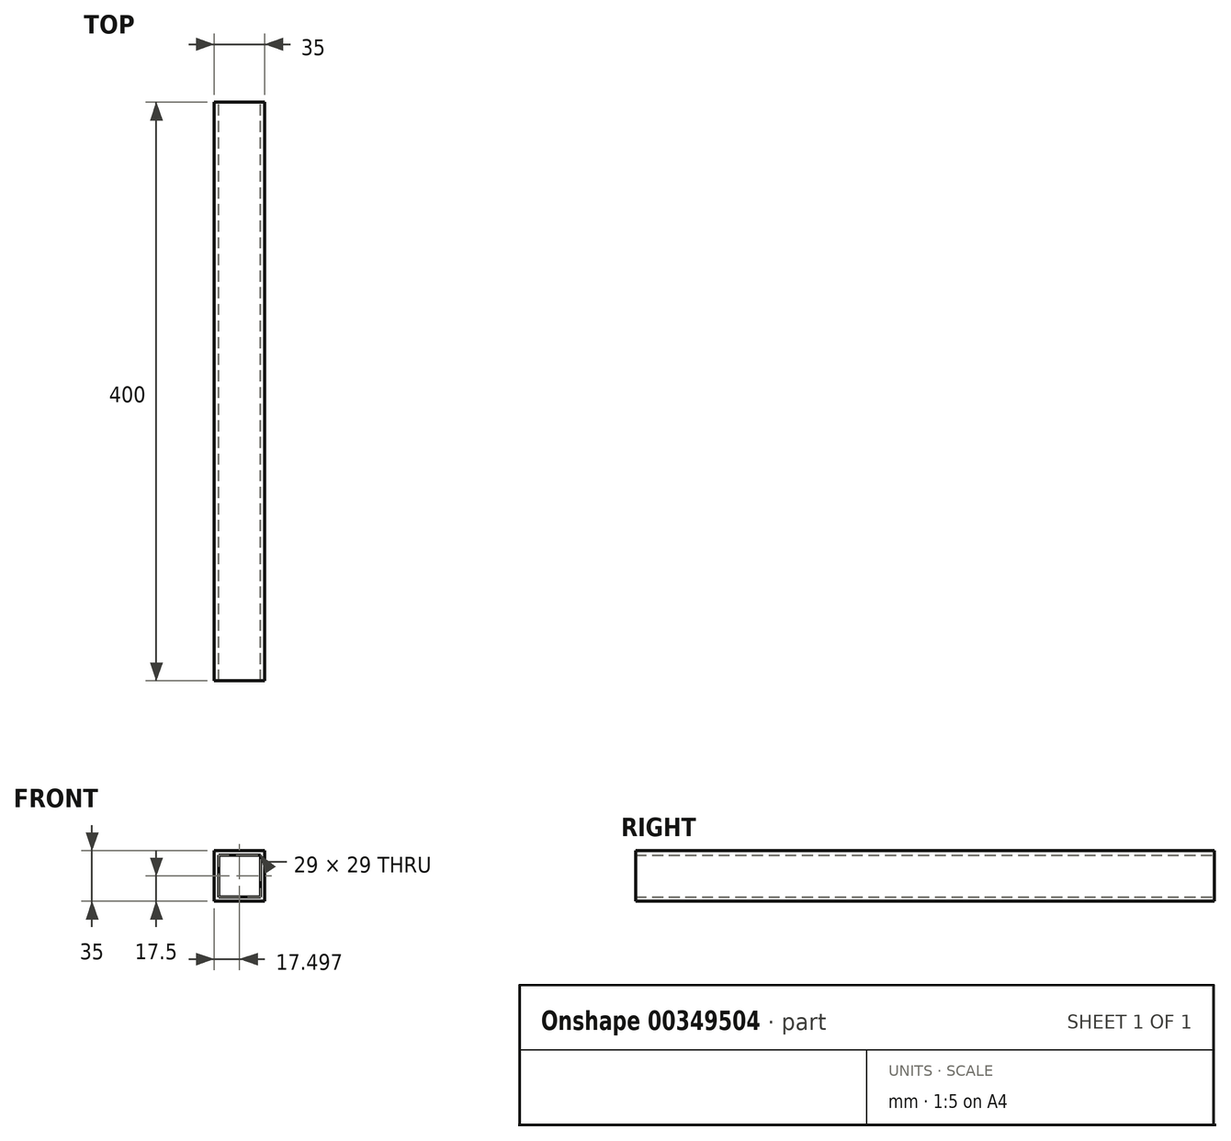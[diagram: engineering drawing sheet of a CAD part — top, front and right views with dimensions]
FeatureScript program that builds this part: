
annotation { "Feature Type Name" : "Feature", "Feature Type Description" : "" }
export const myFeature = defineFeature(function(context is Context, id is Id, definition is map)
    precondition{}
    {
        {
            var Q0;
            Q0=qCreatedBy(makeId("Front.planeOp"),FACE);
            var sketch = newSketch(context, id + "F0", { "sketchPlane" : qUnion([Q0])});
            skLineSegment(sketch, "E0.bottom", {"start": v(-137.1, 10.48) * mm, "end": v(-102.1, 10.48) * mm});
            skLineSegment(sketch, "E0.top", {"start": v(-137.1, -24.52) * mm, "end": v(-102.1, -24.52) * mm});
            skLineSegment(sketch, "E0.left", {"start": v(-137.1, 10.48) * mm, "end": v(-137.1, -24.52) * mm});
            skLineSegment(sketch, "E0.right", {"start": v(-102.1, 10.48) * mm, "end": v(-102.1, -24.52) * mm});
            skLineSegment(sketch, "E1.0", {"start": v(-134.1, -21.52) * mm, "end": v(-105.1, -21.52) * mm});
            skLineSegment(sketch, "E1.1", {"start": v(-134.1, 7.48) * mm, "end": v(-134.1, -21.52) * mm});
            skLineSegment(sketch, "E1.2", {"start": v(-134.1, 7.48) * mm, "end": v(-105.1, 7.48) * mm});
            skLineSegment(sketch, "E1.3", {"start": v(-105.1, 7.48) * mm, "end": v(-105.1, -21.52) * mm});
            skSolve(sketch);
        }
        {
            var Q0;
            Q0=makeQuery(id+"F0.imprint","IMPRINT",FACE,{"disambiguationData":[TD([[makeQuery(id+"F0.imprint","IMPRINT",EDGE,{"derivedFrom":sQuery(id+"F0.wireOp",EDGE,"E0.bottom")}),-1.0]])]});
            extrude(context, id + "F1", {"entities" : qUnion([Q0]), "depth" : 400 * mm, "symmetric" : true});
        }
    });
